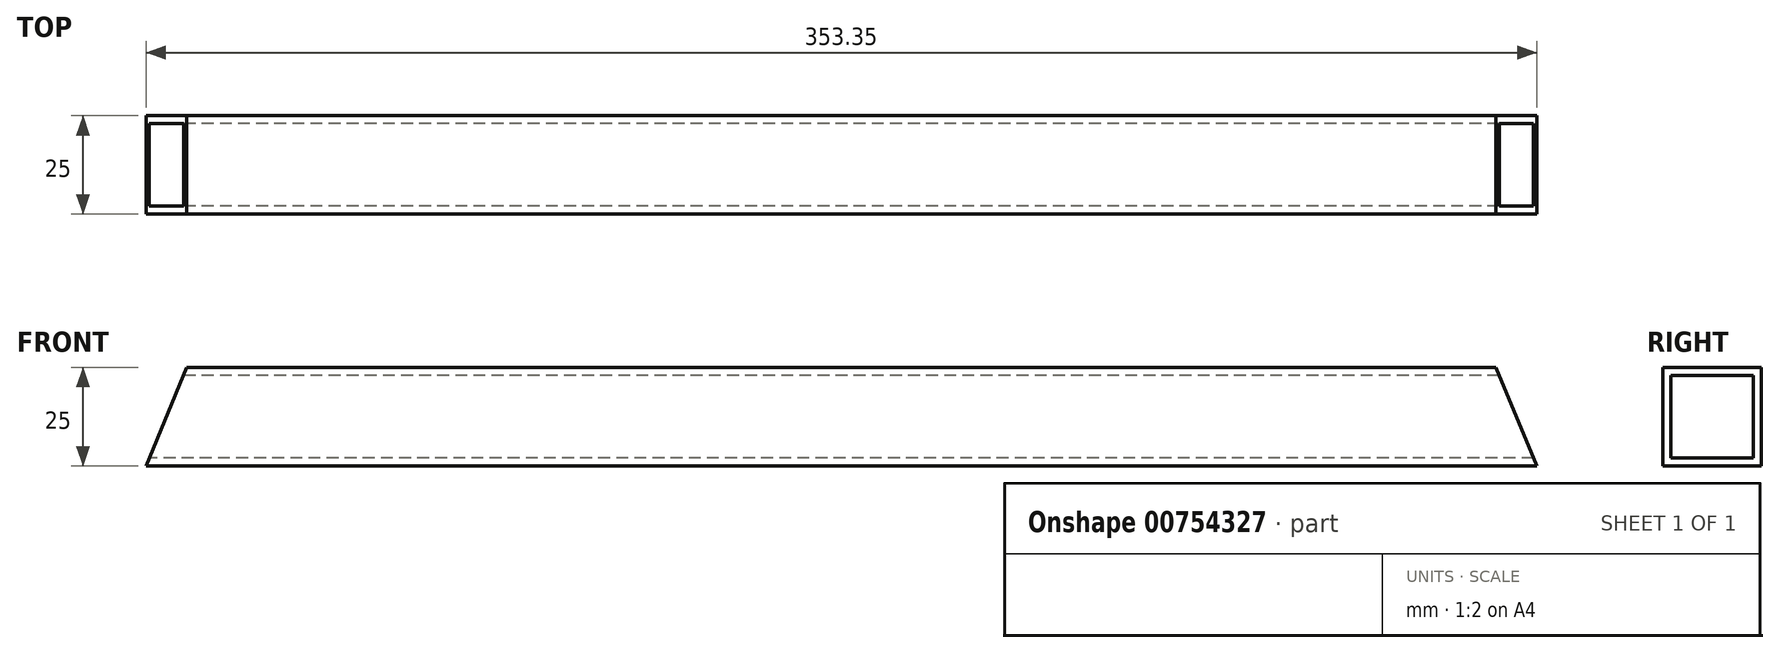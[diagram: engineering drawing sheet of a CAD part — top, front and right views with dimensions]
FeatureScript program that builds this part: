
annotation { "Feature Type Name" : "Feature", "Feature Type Description" : "" }
export const myFeature = defineFeature(function(context is Context, id is Id, definition is map)
    precondition{}
    {
        {
            var Q0;
            Q0=qCreatedBy(makeId("Right.planeOp"),FACE);
            var sketch = newSketch(context, id + "F0", { "sketchPlane" : qUnion([Q0])});
            skLineSegment(sketch, "E0.bottom", {"start": v(12.5, -12.5) * mm, "end": v(-12.5, -12.5) * mm});
            skLineSegment(sketch, "E0.top", {"start": v(12.5, 12.5) * mm, "end": v(-12.5, 12.5) * mm});
            skLineSegment(sketch, "E0.left", {"start": v(12.5, -12.5) * mm, "end": v(12.5, 12.5) * mm});
            skLineSegment(sketch, "E0.right", {"start": v(-12.5, -12.5) * mm, "end": v(-12.5, 12.5) * mm});
            skPoint(sketch, "E0.middle", {"position": v(0, 0) * mm});
            skLineSegment(sketch, "E1.bottom", {"start": v(10.5, 10.5) * mm, "end": v(-10.5, 10.5) * mm});
            skLineSegment(sketch, "E1.top", {"start": v(10.5, -10.5) * mm, "end": v(-10.5, -10.5) * mm});
            skLineSegment(sketch, "E1.left", {"start": v(10.5, 10.5) * mm, "end": v(10.5, -10.5) * mm});
            skLineSegment(sketch, "E1.right", {"start": v(-10.5, 10.5) * mm, "end": v(-10.5, -10.5) * mm});
            skLineSegment(sketch, "E2", {"start": v(-10.5, 10.5) * mm, "end": v(-10.5, 12.5) * mm, "construction": true});
            skLineSegment(sketch, "E3", {"start": v(-10.5, 10.5) * mm, "end": v(-12.5, 10.5) * mm, "construction": true});
            skSolve(sketch);
        }
        {
            var Q0;
            Q0 = qSketchRegion(id + "F0", true);
            extrude(context, id + "F1", {"entities" : qUnion([Q0]), "depth" : 353.35 * mm, "offsetDistance" : 25 * mm});
        }
        {
            var Q0;
            Q0=makeQuery(id+"F1.opExtrude","CAP_EDGE",EDGE,{"disambiguationData":[OSD([sQuery(id+"F0.wireOp",EDGE,"E0.top")])],"isStart":false});
            chamfer(context, id + "F2", {"entities" : qUnion([Q0]), "chamferType" : ChamferType.OFFSET_ANGLE, "width" : 25 * mm, "oppositeDirection" : false, "angle" : 22.5 * degree, "tangentPropagation" : true});
        }
        {
            var Q0;
            Q0=makeQuery(id+"F1.opExtrude","CAP_EDGE",EDGE,{"disambiguationData":[OSD([sQuery(id+"F0.wireOp",EDGE,"E0.top")])],"isStart":true});
            chamfer(context, id + "F3", {"entities" : qUnion([Q0]), "chamferType" : ChamferType.OFFSET_ANGLE, "width" : 25 * mm, "oppositeDirection" : true, "angle" : 22.5 * degree, "tangentPropagation" : true});
        }
    });
